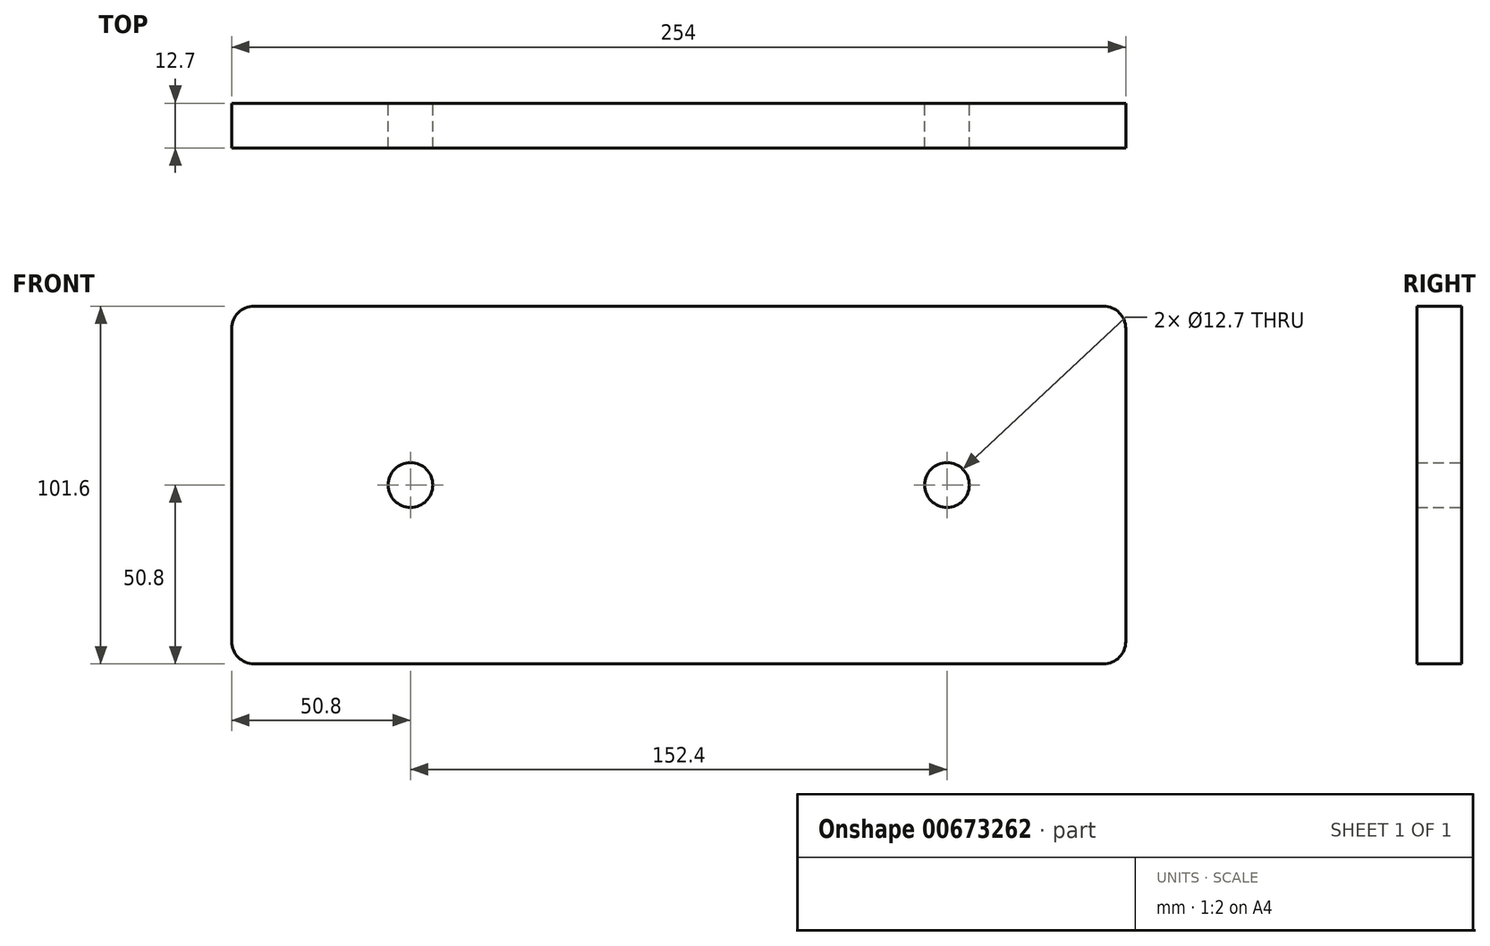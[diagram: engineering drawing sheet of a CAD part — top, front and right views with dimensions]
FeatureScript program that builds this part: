
annotation { "Feature Type Name" : "Feature", "Feature Type Description" : "" }
export const myFeature = defineFeature(function(context is Context, id is Id, definition is map)
    precondition{}
    {
        {
            var Q0;
            Q0=qCreatedBy(makeId("Front.planeOp"),FACE);
            var sketch = newSketch(context, id + "F0", { "sketchPlane" : qUnion([Q0])});
            skLineSegment(sketch, "E0.bottom", {"start": v(0, 0) * mm, "end": v(254, 0) * mm});
            skLineSegment(sketch, "E0.top", {"start": v(0, 101.6) * mm, "end": v(254, 101.6) * mm});
            skLineSegment(sketch, "E0.left", {"start": v(0, 0) * mm, "end": v(0, 101.6) * mm});
            skLineSegment(sketch, "E0.right", {"start": v(254, 0) * mm, "end": v(254, 101.6) * mm});
            skPoint(sketch, "E1", {"position": v(50.8, 50.8) * mm});
            skPoint(sketch, "E2", {"position": v(203.2, 50.8) * mm});
            skSolve(sketch);
        }
        {
            var Q0;
            Q0=qSketchRegion(id+"F0",true);
            extrude(context, id + "F1", {"entities" : qUnion([Q0]), "depth" : 12.7 * mm});
        }
        {
            var Q0;
            Q0=sQuery(id+"F0.wireOp",VERTEX,"E2");
            var Q1;
            Q1=sQuery(id+"F0.wireOp",VERTEX,"E1");
            var Q2;
            Q2=makeQuery(id+"F1.opExtrude","SWEPT_BODY",BODY,{"disambiguationData":[OSD([sQuery(id+"F0.wireOp",EDGE,"E0.bottom"),sQuery(id+"F0.wireOp",EDGE,"E0.top"),sQuery(id+"F0.wireOp",EDGE,"E0.left"),sQuery(id+"F0.wireOp",EDGE,"E0.right")])]});
            hole(context, id + "F2", {"style" : HoleStyle.SIMPLE, "endStyle" : HoleEndStyle.THROUGH, "oppositeDirection" : true, "holeDiameter" : 12.7 * mm, "isTappedThrough" : true, "tappedDepth" : 12.7 * mm, "tapClearance" : 3, "locations" : qUnion([Q0, Q1]), "scope" : qUnion([Q2])});
        }
        {
            var Q0;
            Q0=makeQuery(id+"F1.opExtrude","SWEPT_EDGE",EDGE,{"disambiguationData":[OSD([sQuery(id+"F0.wireOp",EDGE,"E0.top"),sQuery(id+"F0.wireOp",EDGE,"E0.right")])]});
            var Q1;
            Q1=makeQuery(id+"F1.opExtrude","SWEPT_EDGE",EDGE,{"disambiguationData":[OSD([sQuery(id+"F0.wireOp",EDGE,"E0.bottom"),sQuery(id+"F0.wireOp",EDGE,"E0.right")])]});
            var Q2;
            Q2=makeQuery(id+"F1.opExtrude","SWEPT_EDGE",EDGE,{"disambiguationData":[OSD([sQuery(id+"F0.wireOp",EDGE,"E0.bottom"),sQuery(id+"F0.wireOp",EDGE,"E0.left")])]});
            var Q3;
            Q3=makeQuery(id+"F1.opExtrude","SWEPT_EDGE",EDGE,{"disambiguationData":[OSD([sQuery(id+"F0.wireOp",EDGE,"E0.top"),sQuery(id+"F0.wireOp",EDGE,"E0.left")])]});
            fillet(context, id + "F3", {"entities" : qUnion([Q0, Q1, Q2, Q3]), "radius" : 6.35 * mm, "tangentPropagation" : true, "allowEdgeOverflow" : false});
        }
    });
